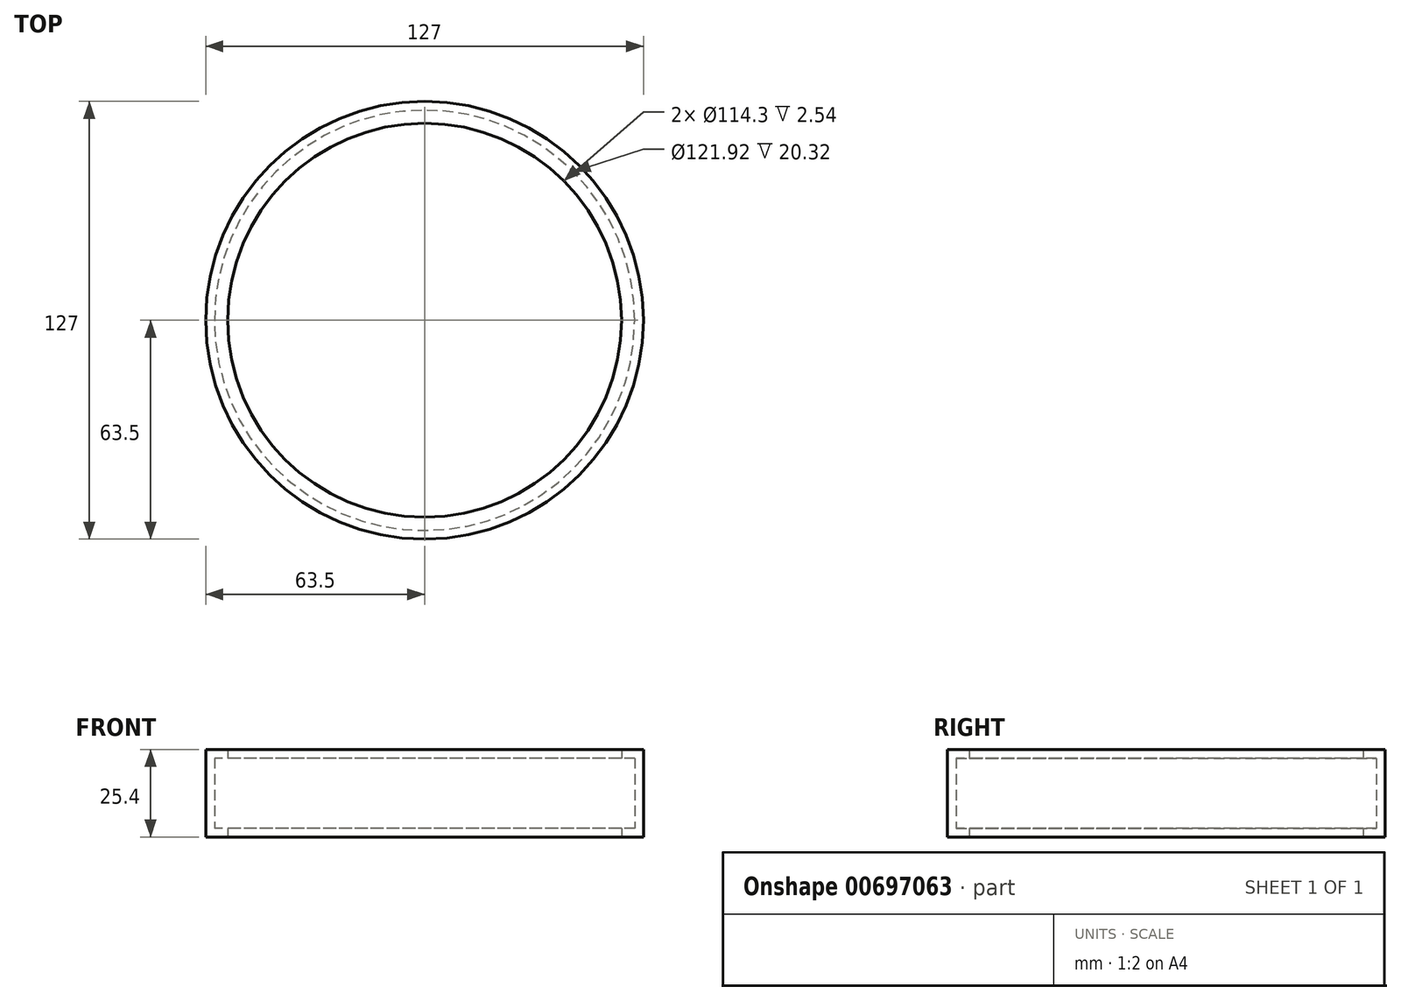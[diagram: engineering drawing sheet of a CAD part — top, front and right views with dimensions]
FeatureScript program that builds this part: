
annotation { "Feature Type Name" : "Feature", "Feature Type Description" : "" }
export const myFeature = defineFeature(function(context is Context, id is Id, definition is map)
    precondition{}
    {
        {
            var Q0;
            Q0=qCreatedBy(makeId("Top.planeOp"),FACE);
            var sketch = newSketch(context, id + "F0", { "sketchPlane" : qUnion([Q0])});
            skCircle(sketch, "E0", {"center": v(0, 0) * mm, "radius": 63.5 * mm});
            skCircle(sketch, "E1", {"center": v(0, 0) * mm, "radius": 57.15 * mm});
            skSolve(sketch);
        }
        {
            var Q0;
            Q0=makeQuery(id+"F0.imprint","IMPRINT",FACE,{"disambiguationData":[TD([[makeQuery(id+"F0.imprint","IMPRINT",EDGE,{"derivedFrom":sQuery(id+"F0.wireOp",EDGE,"E0")}),1.0]])]});
            extrude(context, id + "F1", {"entities" : qUnion([Q0]), "depth" : 25.4 * mm, "offsetDistance" : 25.4 * mm});
        }
        {
            var Q0;
            Q0=makeQuery(id+"F1.opExtrude","SWEPT_FACE",FACE,{"disambiguationData":[OSD([sQuery(id+"F0.wireOp",EDGE,"E1")])]});
            shell(context, id + "F2", {"entities" : qUnion([Q0]), "thickness" : 2.54 * mm});
        }
    });
